# Revit family: QF_ELECTROLUXPROFESSIONAL_505080_EHT8M6
name_source: partatom
category: Specialty Equipment
revit_build: Autodesk Revit 2018 (Build: 20190510_1515(x64)
units: mm (PartAtom-declared; Revit-internal decimal feet)

## family parameters
Always vertical = Yes
Cut with Voids When Loaded = No
Part Type = Normal
Room Calculation Point = No
Round Connector Dimension = Use Diameter
Shared = Yes
Work Plane-Based = No

## types (1)
- QF_ELECTROLUXPROFESSIONAL_505080_EHT8M6
    Apparent Power = 0 VA
    Cold Water Connection Height = 0 mm  [stored 0 ft]
    Cold Water Flow = 0 GPM
    Cold Water Maximum Pressure = 0.00 psi
    Cold Water Minimum Pressure = 0.00 psi
    Cold Water Size = 1"
    Cold Water Temperature Recommended = -460 °F
    Conn Conduit = Yes
    Cycle = 60 Hz
    Description = HOOD TYPE DISHWASHER,80R/H-MAR.440V/60HZ
    Direct Waste Size = 1"
    Electrical Remarks = 440 V/3 ph/60 Hz
    FL Amps = 0 A
    HP = 13.3 HP
    Indirect Waste Connection Height = 0 mm  [stored 0 ft]
    Indirect Waste Radius Size = 10 mm  [stored 0.0328084 ft]
    Indirect Waste Size = 1"
    Manufacturer = ELECTROLUX
    Max Overcurrent Protection = 0 A
    Min Ckt Ampacity = 0 A
    Model = 505080
    Phase = 3
    URL = www.electrolux.com/foodservice
    URL Cutsheet = www.electrolux.com/foodservice
    URL Manufacturer = www.electrolux.com/foodservice
    Volts = 440 V
    Watts = 0 W
    Weight = 106 kg

note: [stored X ft] marks values corroborated as IEEE doubles in the binary element streams (Revit-internal decimal feet)

## geometry (parser evidence)
native form markers: Blend x12, Sweep x2
no freeform markers — native parametric forms only
